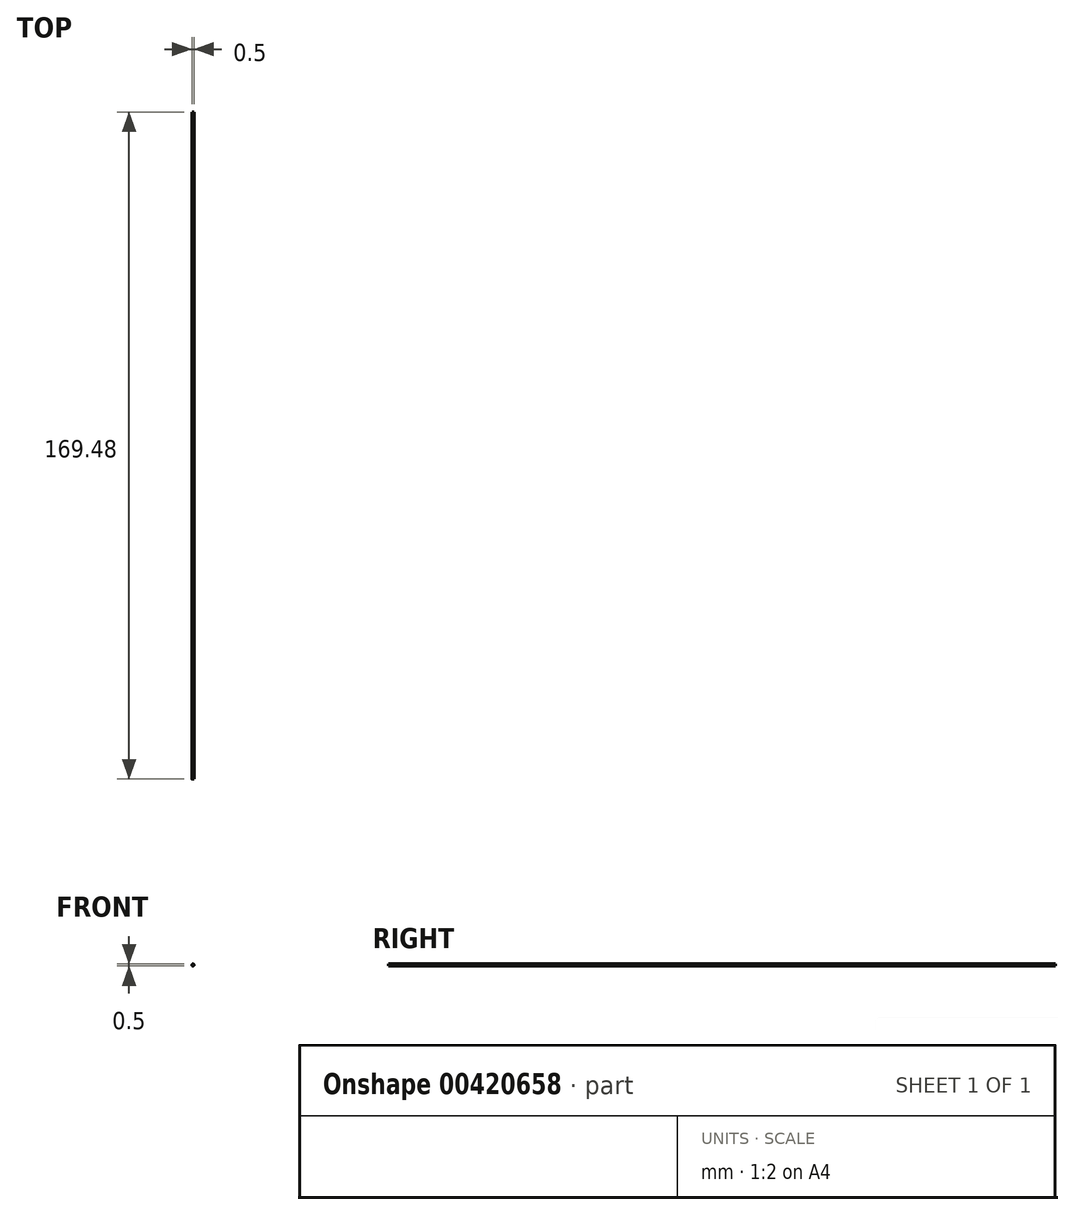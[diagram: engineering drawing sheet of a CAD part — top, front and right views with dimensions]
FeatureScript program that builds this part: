
annotation { "Feature Type Name" : "Feature", "Feature Type Description" : "" }
export const myFeature = defineFeature(function(context is Context, id is Id, definition is map)
    precondition{}
    {
        {
            var Q0;
            Q0=qCreatedBy(makeId("Front.planeOp"),FACE);
            var sketch = newSketch(context, id + "F0", { "sketchPlane" : qUnion([Q0])});
            skCircle(sketch, "E0", {"center": v(0, 0) * mm, "radius": 0.25 * mm});
            skSolve(sketch);
        }
        {
            var Q0;
            Q0 = qSketchRegion(id + "F0", true);
            extrude(context, id + "F1", {"entities" : qUnion([Q0]), "depth" : 169.48 * mm});
        }
    });
